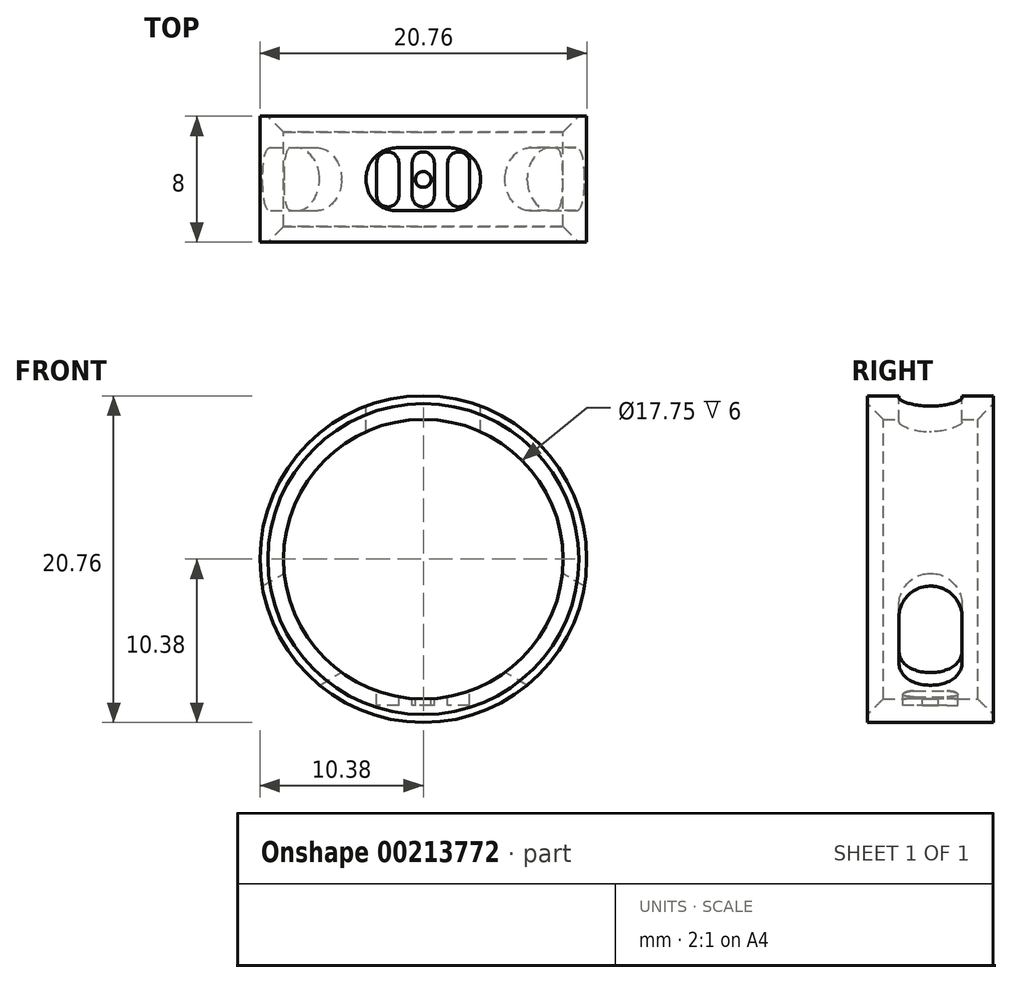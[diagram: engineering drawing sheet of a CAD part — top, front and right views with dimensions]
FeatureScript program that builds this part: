
annotation { "Feature Type Name" : "Feature", "Feature Type Description" : "" }
export const myFeature = defineFeature(function(context is Context, id is Id, definition is map)
    precondition{}
    {
        {
            var Q0;
            Q0=qCreatedBy(makeId("Front.planeOp"),FACE);
            var sketch = newSketch(context, id + "F0", { "sketchPlane" : qUnion([Q0])});
            skCircle(sketch, "E0", {"center": v(0, 0) * mm, "radius": 8.88 * mm});
            skCircle(sketch, "E1.0", {"center": v(0, 0) * mm, "radius": 10.38 * mm});
            skLineSegment(sketch, "E2.bottom", {"start": v(3.63, 9.72) * mm, "end": v(-3.63, 9.72) * mm, "construction": true});
            skLineSegment(sketch, "E2.top", {"start": v(3.63, 11.88) * mm, "end": v(-3.63, 11.88) * mm});
            skLineSegment(sketch, "E2.left", {"start": v(3.63, 9.72) * mm, "end": v(3.63, 11.88) * mm});
            skLineSegment(sketch, "E2.right", {"start": v(-3.63, 9.72) * mm, "end": v(-3.63, 11.88) * mm});
            skPoint(sketch, "E2.middle", {"position": v(0, 10.8) * mm});
            skLineSegment(sketch, "E3.1.0", {"start": v(-6.6, -8) * mm, "end": v(-8.47, -9.08) * mm});
            skLineSegment(sketch, "E3.1.1", {"start": v(-10.23, -1.71) * mm, "end": v(-12.1, -2.8) * mm});
            skLineSegment(sketch, "E3.1.2", {"start": v(-12.1, -2.8) * mm, "end": v(-8.47, -9.08) * mm});
            skLineSegment(sketch, "E3.1.3", {"start": v(-10.23, -1.71) * mm, "end": v(-6.6, -8) * mm, "construction": true});
            skLineSegment(sketch, "E3.2.0", {"start": v(10.23, -1.71) * mm, "end": v(12.1, -2.8) * mm});
            skLineSegment(sketch, "E3.2.1", {"start": v(6.6, -8) * mm, "end": v(8.47, -9.08) * mm});
            skLineSegment(sketch, "E3.2.2", {"start": v(8.47, -9.08) * mm, "end": v(12.1, -2.8) * mm});
            skLineSegment(sketch, "E3.2.3", {"start": v(6.6, -8) * mm, "end": v(10.23, -1.71) * mm, "construction": true});
            skLineSegment(sketch, "E4", {"start": v(0, 0) * mm, "end": v(7.34, 7.34) * mm, "construction": true});
            skLineSegment(sketch, "E5", {"start": v(0, 0) * mm, "end": v(-7.34, 7.34) * mm, "construction": true});
            skLineSegment(sketch, "E6.MirrorCS", {"start": v(0, 0) * mm, "end": v(7.34, -7.34) * mm, "construction": true});
            skLineSegment(sketch, "E7.MirrorCS", {"start": v(0, 0) * mm, "end": v(-7.34, -7.34) * mm, "construction": true});
            skLineSegment(sketch, "E8.0", {"start": v(-0.14, 0.14) * mm, "end": v(0, 0.28) * mm});
            skLineSegment(sketch, "E9.MirrorCS", {"start": v(0.14, -0.14) * mm, "end": v(0.28, 0) * mm});
            skLineSegment(sketch, "E10.MirrorCS", {"start": v(0.14, 0.14) * mm, "end": v(0, 0.28) * mm});
            skLineSegment(sketch, "E11.MirrorCS", {"start": v(-0.14, -0.14) * mm, "end": v(-0.28, 0) * mm});
            skLineSegment(sketch, "E12.MirrorCS", {"start": v(0.14, 0.14) * mm, "end": v(0.28, 0) * mm});
            skLineSegment(sketch, "E13.MirrorCS", {"start": v(-0.14, -0.14) * mm, "end": v(0, -0.28) * mm});
            skLineSegment(sketch, "E14.MirrorCS", {"start": v(0.14, -0.14) * mm, "end": v(0, -0.28) * mm});
            skLineSegment(sketch, "E15.MirrorCS", {"start": v(-0.14, 0.14) * mm, "end": v(-0.28, 0) * mm});
            skLineSegment(sketch, "E16.trimOffspring", {"start": v(-6.13, -6.42) * mm, "end": v(-7.2, -7.48) * mm, "construction": true});
            skLineSegment(sketch, "E17.trimOffspring", {"start": v(-6.42, -6.13) * mm, "end": v(-7.48, -7.2) * mm, "construction": true});
            skLineSegment(sketch, "E18.trimOffspring", {"start": v(-6.42, 6.13) * mm, "end": v(-7.48, 7.2) * mm, "construction": true});
            skLineSegment(sketch, "E19.trimOffspring", {"start": v(-6.13, 6.42) * mm, "end": v(-7.2, 7.48) * mm, "construction": true});
            skLineSegment(sketch, "E20.trimOffspring", {"start": v(6.13, 6.42) * mm, "end": v(7.2, 7.48) * mm, "construction": true});
            skLineSegment(sketch, "E21.trimOffspring", {"start": v(6.42, 6.13) * mm, "end": v(7.48, 7.2) * mm, "construction": true});
            skLineSegment(sketch, "E22.trimOffspring", {"start": v(6.13, -6.42) * mm, "end": v(7.2, -7.48) * mm, "construction": true});
            skLineSegment(sketch, "E23.trimOffspring", {"start": v(6.42, -6.13) * mm, "end": v(7.48, -7.2) * mm, "construction": true});
            skLineSegment(sketch, "E24", {"start": v(-3.63, 9.72) * mm, "end": v(-3.63, 6.6) * mm});
            skLineSegment(sketch, "E25", {"start": v(-3.63, 6.6) * mm, "end": v(3.63, 6.6) * mm});
            skLineSegment(sketch, "E26", {"start": v(3.63, 6.6) * mm, "end": v(3.63, 9.72) * mm});
            skLineSegment(sketch, "E27", {"start": v(10.23, -1.71) * mm, "end": v(7.27, 0) * mm});
            skLineSegment(sketch, "E28", {"start": v(6.6, -8) * mm, "end": v(3.35, -6.13) * mm});
            skLineSegment(sketch, "E29", {"start": v(3.35, -6.13) * mm, "end": v(7.27, 0) * mm});
            skLineSegment(sketch, "E30", {"start": v(-6.6, -8) * mm, "end": v(-3.28, -6.1) * mm});
            skLineSegment(sketch, "E31", {"start": v(-10.23, -1.71) * mm, "end": v(-6.86, 0.24) * mm});
            skLineSegment(sketch, "E32", {"start": v(-6.86, 0.24) * mm, "end": v(-3.28, -6.1) * mm});
            skSolve(sketch);
        }
        {
            var Q0;
            Q0=makeQuery(id+"F0.imprint","IMPRINT",FACE,{"disambiguationData":[TD([[makeQuery(id+"F0.imprint","IMPRINT",EDGE,{"derivedFrom":sQuery(id+"F0.wireOp",EDGE,"E0")}),-1.0]])]});
            var Q1;
            {var subQ2=sQuery(id+"F0.wireOp",EDGE,"E16.trimOffspring");var subQ7=sQuery(id+"F0.wireOp",EDGE,"E0");var subQ9=makeQuery(id+"F0.imprint","INTERSECT",VERTEX,{"derivedFrom":[subQ7,subQ2]});Q1=makeQuery(id+"F0.imprint","IMPRINT",FACE,{"disambiguationData":[TD([[makeQuery(id+"F0.imprint","IMPRINT",EDGE,{"disambiguationData":[TD([[subQ9,-1.0]])],"derivedFrom":subQ7}),-1.0]])]});}
            var Q2;
            {var subQ5=sQuery(id+"F0.wireOp",EDGE,"E21.trimOffspring");var subQ7=sQuery(id+"F0.wireOp",EDGE,"E0");var subQ8=makeQuery(id+"F0.imprint","INTERSECT",VERTEX,{"derivedFrom":[subQ7,subQ5]});Q2=makeQuery(id+"F0.imprint","IMPRINT",FACE,{"disambiguationData":[TD([[makeQuery(id+"F0.imprint","IMPRINT",EDGE,{"disambiguationData":[TD([[subQ8,1.0]])],"derivedFrom":subQ7}),-1.0]])]});}
            var Q3;
            {var subQ2=sQuery(id+"F0.wireOp",EDGE,"E19.trimOffspring");var subQ7=sQuery(id+"F0.wireOp",EDGE,"E0");var subQ8=makeQuery(id+"F0.imprint","INTERSECT",VERTEX,{"derivedFrom":[subQ7,subQ2]});Q3=makeQuery(id+"F0.imprint","IMPRINT",FACE,{"disambiguationData":[TD([[makeQuery(id+"F0.imprint","IMPRINT",EDGE,{"disambiguationData":[TD([[subQ8,1.0]])],"derivedFrom":subQ7}),-1.0]])]});}
            var Q4;
            {var subQ5=sQuery(id+"F0.wireOp",EDGE,"E17.trimOffspring");var subQ6=sQuery(id+"F0.wireOp",EDGE,"E0");var subQ7=makeQuery(id+"F0.imprint","INTERSECT",VERTEX,{"derivedFrom":[subQ6,subQ5]});Q4=makeQuery(id+"F0.imprint","IMPRINT",FACE,{"disambiguationData":[TD([[makeQuery(id+"F0.imprint","IMPRINT",EDGE,{"disambiguationData":[TD([[subQ7,1.0]])],"derivedFrom":subQ6}),-1.0]])]});}
            extrude(context, id + "F1", {"entities" : qUnion([Q0, Q1, Q2, Q3, Q4]), "depth" : 4 * mm, "hasSecondDirection" : true, "secondDirectionOppositeDirection" : true, "secondDirectionDepth" : 4 * mm});
        }
        {
            var Q0;
            Q0=makeQuery(id+"F1.opExtrude","CAP_EDGE",EDGE,{"disambiguationData":[OSD([sQuery(id+"F0.wireOp",EDGE,"E0")])],"isStart":false});
            var Q1;
            Q1=makeQuery(id+"F1.opExtrude","CAP_EDGE",EDGE,{"disambiguationData":[OSD([sQuery(id+"F0.wireOp",EDGE,"E0")])],"isStart":true});
            chamfer(context, id + "F2", {"entities" : qUnion([Q0, Q1]), "width" : 1 * mm, "tangentPropagation" : true});
        }
        {
            var Q0;
            Q0=qCreatedBy(makeId("Top.planeOp"),FACE);
            var sketch = newSketch(context, id + "F3", { "sketchPlane" : qUnion([Q0])});
            skCircle(sketch, "E33", {"center": v(0, 0) * mm, "radius": 0.15 * mm});
            skCircle(sketch, "E34.1.0.0", {"center": v(0, -0.6) * mm, "radius": 0.15 * mm});
            skCircle(sketch, "E34.2.0.0", {"center": v(0, -1.2) * mm, "radius": 0.15 * mm});
            skCircle(sketch, "E34.3.0.0", {"center": v(0, -1.8) * mm, "radius": 0.15 * mm});
            skCircle(sketch, "E34.4.0.0", {"center": v(0, -2.4) * mm, "radius": 0.15 * mm});
            skCircle(sketch, "E34.5.0.0", {"center": v(0, -3) * mm, "radius": 0.15 * mm});
            skCircle(sketch, "E34.6.0.0", {"center": v(0, -3.6) * mm, "radius": 0.15 * mm});
            skLineSegment(sketch, "E34.direction1", {"start": v(0, 0) * mm, "end": v(0, -0.6) * mm, "construction": true});
            skCircle(sketch, "E35.MirrorC", {"center": v(0, 0.6) * mm, "radius": 0.15 * mm});
            skCircle(sketch, "E36.MirrorC", {"center": v(0, 1.2) * mm, "radius": 0.15 * mm});
            skCircle(sketch, "E37.MirrorC", {"center": v(0, 1.8) * mm, "radius": 0.15 * mm});
            skCircle(sketch, "E38.MirrorC", {"center": v(0, 2.4) * mm, "radius": 0.15 * mm});
            skCircle(sketch, "E39.MirrorC", {"center": v(0, 3) * mm, "radius": 0.15 * mm});
            skCircle(sketch, "E40.MirrorC", {"center": v(0, 3.6) * mm, "radius": 0.15 * mm});
            skSolve(sketch);
        }
        {
            var Q0;
            Q0=makeQuery(id+"F0.imprint","IMPRINT",FACE,{"disambiguationData":[TD([[makeQuery(id+"F0.imprint","IMPRINT",EDGE,{"derivedFrom":sQuery(id+"F0.wireOp",EDGE,"E2.top")}),1.0]])]});
            var Q1;
            {var subQ0=sQuery(id+"F0.wireOp",EDGE,"E24");var subQ1=sQuery(id+"F0.wireOp",EDGE,"E0");var subQ2=makeQuery(id+"F0.imprint","INTERSECT",VERTEX,{"derivedFrom":[subQ1,subQ0]});Q1=makeQuery(id+"F0.imprint","IMPRINT",FACE,{"disambiguationData":[TD([[makeQuery(id+"F0.imprint","IMPRINT",EDGE,{"disambiguationData":[TD([[subQ2,1.0]])],"derivedFrom":subQ1}),-1.0]])]});}
            var Q2;
            {var subQ5=sQuery(id+"F0.wireOp",EDGE,"E25");Q2=makeQuery(id+"F0.imprint","IMPRINT",FACE,{"disambiguationData":[TD([[makeQuery(id+"F0.imprint","IMPRINT",EDGE,{"derivedFrom":subQ5}),1.0]])]});}
            var Q3;
            {var subQ5=sQuery(id+"F0.wireOp",EDGE,"E29");Q3=makeQuery(id+"F0.imprint","IMPRINT",FACE,{"disambiguationData":[TD([[makeQuery(id+"F0.imprint","IMPRINT",EDGE,{"derivedFrom":subQ5}),-1.0]])]});}
            var Q4;
            {var subQ0=sQuery(id+"F0.wireOp",EDGE,"E28");var subQ1=sQuery(id+"F0.wireOp",EDGE,"E0");var subQ2=makeQuery(id+"F0.imprint","INTERSECT",VERTEX,{"derivedFrom":[subQ1,subQ0]});Q4=makeQuery(id+"F0.imprint","IMPRINT",FACE,{"disambiguationData":[TD([[makeQuery(id+"F0.imprint","IMPRINT",EDGE,{"disambiguationData":[TD([[subQ2,-1.0]])],"derivedFrom":subQ1}),-1.0]])]});}
            var Q5;
            {var subQ0=sQuery(id+"F0.wireOp",EDGE,"E3.2.0");Q5=makeQuery(id+"F0.imprint","IMPRINT",FACE,{"disambiguationData":[TD([[makeQuery(id+"F0.imprint","IMPRINT",EDGE,{"derivedFrom":subQ0}),-1.0]])]});}
            var Q6;
            {var subQ5=sQuery(id+"F0.wireOp",EDGE,"E32");Q6=makeQuery(id+"F0.imprint","IMPRINT",FACE,{"disambiguationData":[TD([[makeQuery(id+"F0.imprint","IMPRINT",EDGE,{"derivedFrom":subQ5}),-1.0]])]});}
            var Q7;
            {var subQ0=sQuery(id+"F0.wireOp",EDGE,"E3.1.0");Q7=makeQuery(id+"F0.imprint","IMPRINT",FACE,{"disambiguationData":[TD([[makeQuery(id+"F0.imprint","IMPRINT",EDGE,{"derivedFrom":subQ0}),-1.0]])]});}
            var Q8;
            {var subQ0=sQuery(id+"F0.wireOp",EDGE,"E31");var subQ1=sQuery(id+"F0.wireOp",EDGE,"E0");var subQ2=makeQuery(id+"F0.imprint","INTERSECT",VERTEX,{"derivedFrom":[subQ1,subQ0]});Q8=makeQuery(id+"F0.imprint","IMPRINT",FACE,{"disambiguationData":[TD([[makeQuery(id+"F0.imprint","IMPRINT",EDGE,{"disambiguationData":[TD([[subQ2,-1.0]])],"derivedFrom":subQ1}),-1.0]])]});}
            extrude(context, id + "F4", {"entities" : qUnion([Q0, Q1, Q2, Q3, Q4, Q5, Q6, Q7, Q8]), "operationType" : NewBodyOperationType.REMOVE, "oppositeDirection" : true, "depth" : 2 * mm, "hasSecondDirection" : true, "secondDirectionOppositeDirection" : false, "secondDirectionDepth" : 2 * mm});
        }
        {
            var Q0;
            Q0=makeQuery(id+"F4.boolean.opBoolean","COPY",EDGE,{"derivedFrom":makeQuery(id+"F4.opExtrude","CAP_EDGE",EDGE,{"disambiguationData":[OSD([sQuery(id+"F0.wireOp",EDGE,"E3.2.1"),sQuery(id+"F0.wireOp",EDGE,"E28")])],"isStart":false})});
            var Q1;
            Q1=makeQuery(id+"F4.boolean.opBoolean","COPY",EDGE,{"derivedFrom":makeQuery(id+"F4.opExtrude","CAP_EDGE",EDGE,{"disambiguationData":[OSD([sQuery(id+"F0.wireOp",EDGE,"E3.2.0"),sQuery(id+"F0.wireOp",EDGE,"E27")])],"isStart":false})});
            var Q2;
            Q2=makeQuery(id+"F4.boolean.opBoolean","COPY",EDGE,{"derivedFrom":makeQuery(id+"F4.opExtrude","CAP_EDGE",EDGE,{"disambiguationData":[OSD([sQuery(id+"F0.wireOp",EDGE,"E3.2.0"),sQuery(id+"F0.wireOp",EDGE,"E27")])],"isStart":true})});
            var Q3;
            Q3=makeQuery(id+"F4.boolean.opBoolean","COPY",EDGE,{"derivedFrom":makeQuery(id+"F4.opExtrude","CAP_EDGE",EDGE,{"disambiguationData":[OSD([sQuery(id+"F0.wireOp",EDGE,"E3.2.1"),sQuery(id+"F0.wireOp",EDGE,"E28")])],"isStart":true})});
            var Q4;
            Q4=makeQuery(id+"F4.boolean.opBoolean","COPY",EDGE,{"derivedFrom":makeQuery(id+"F4.opExtrude","CAP_EDGE",EDGE,{"disambiguationData":[OSD([sQuery(id+"F0.wireOp",EDGE,"E3.1.0"),sQuery(id+"F0.wireOp",EDGE,"E30")])],"isStart":false})});
            var Q5;
            Q5=makeQuery(id+"F4.boolean.opBoolean","COPY",EDGE,{"derivedFrom":makeQuery(id+"F4.opExtrude","CAP_EDGE",EDGE,{"disambiguationData":[OSD([sQuery(id+"F0.wireOp",EDGE,"E3.1.1"),sQuery(id+"F0.wireOp",EDGE,"E31")])],"isStart":false})});
            var Q6;
            Q6=makeQuery(id+"F4.boolean.opBoolean","COPY",EDGE,{"derivedFrom":makeQuery(id+"F4.opExtrude","CAP_EDGE",EDGE,{"disambiguationData":[OSD([sQuery(id+"F0.wireOp",EDGE,"E3.1.1"),sQuery(id+"F0.wireOp",EDGE,"E31")])],"isStart":true})});
            var Q7;
            Q7=makeQuery(id+"F4.boolean.opBoolean","COPY",EDGE,{"derivedFrom":makeQuery(id+"F4.opExtrude","CAP_EDGE",EDGE,{"disambiguationData":[OSD([sQuery(id+"F0.wireOp",EDGE,"E3.1.0"),sQuery(id+"F0.wireOp",EDGE,"E30")])],"isStart":true})});
            var Q8;
            Q8=makeQuery(id+"F4.boolean.opBoolean","COPY",EDGE,{"derivedFrom":makeQuery(id+"F4.opExtrude","CAP_EDGE",EDGE,{"disambiguationData":[OSD([sQuery(id+"F0.wireOp",EDGE,"E2.right"),sQuery(id+"F0.wireOp",EDGE,"E24")])],"isStart":false})});
            var Q9;
            Q9=makeQuery(id+"F4.boolean.opBoolean","COPY",EDGE,{"derivedFrom":makeQuery(id+"F4.opExtrude","CAP_EDGE",EDGE,{"disambiguationData":[OSD([sQuery(id+"F0.wireOp",EDGE,"E2.left"),sQuery(id+"F0.wireOp",EDGE,"E26")])],"isStart":false})});
            var Q10;
            Q10=makeQuery(id+"F4.boolean.opBoolean","COPY",EDGE,{"derivedFrom":makeQuery(id+"F4.opExtrude","CAP_EDGE",EDGE,{"disambiguationData":[OSD([sQuery(id+"F0.wireOp",EDGE,"E2.right"),sQuery(id+"F0.wireOp",EDGE,"E24")])],"isStart":true})});
            var Q11;
            Q11=makeQuery(id+"F4.boolean.opBoolean","COPY",EDGE,{"derivedFrom":makeQuery(id+"F4.opExtrude","CAP_EDGE",EDGE,{"disambiguationData":[OSD([sQuery(id+"F0.wireOp",EDGE,"E2.left"),sQuery(id+"F0.wireOp",EDGE,"E26")])],"isStart":true})});
            fillet(context, id + "F5", {"entities" : qUnion([Q0, Q1, Q2, Q3, Q4, Q5, Q6, Q7, Q8, Q9, Q10, Q11]), "radius" : 1.94 * mm, "tangentPropagation" : true, "allowEdgeOverflow" : false});
        }
        {
            var Q0;
            Q0=qCreatedBy(makeId("Top.planeOp"),FACE);
            var sketch = newSketch(context, id + "F6", { "sketchPlane" : qUnion([Q0])});
            skLineSegment(sketch, "E41.bottom", {"start": v(-0.7, 1.04) * mm, "end": v(-0.7, -1.05) * mm});
            skArc(sketch, "E42.filletArc", {"start": v(0.7, 1.04) * mm, "mid": v(0.49, 1.54) * mm, "end": v(0, 1.74) * mm});
            skArc(sketch, "E43.filletArc", {"start": v(0, 1.74) * mm, "mid": v(-0.5, 1.54) * mm, "end": v(-0.7, 1.04) * mm});
            skArc(sketch, "E44.filletArc", {"start": v(0, -1.75) * mm, "mid": v(0.49, -1.54) * mm, "end": v(0.7, -1.05) * mm});
            skArc(sketch, "E45.filletArc", {"start": v(-0.7, -1.05) * mm, "mid": v(-0.5, -1.54) * mm, "end": v(0, -1.75) * mm});
            skLineSegment(sketch, "E46.bottom", {"start": v(-2.96, 1.04) * mm, "end": v(-2.96, -1.05) * mm});
            skLineSegment(sketch, "E46.top", {"start": v(-1.56, 1.04) * mm, "end": v(-1.56, -1.05) * mm});
            skArc(sketch, "E47.filletArc", {"start": v(-1.56, 1.04) * mm, "mid": v(-1.76, 1.54) * mm, "end": v(-2.26, 1.74) * mm});
            skArc(sketch, "E48.filletArc", {"start": v(-2.26, 1.74) * mm, "mid": v(-2.75, 1.54) * mm, "end": v(-2.96, 1.04) * mm});
            skArc(sketch, "E49.filletArc", {"start": v(-2.26, -1.75) * mm, "mid": v(-1.76, -1.54) * mm, "end": v(-1.56, -1.05) * mm});
            skArc(sketch, "E50.filletArc", {"start": v(-2.96, -1.05) * mm, "mid": v(-2.75, -1.54) * mm, "end": v(-2.26, -1.75) * mm});
            skLineSegment(sketch, "E51", {"start": v(0.7, 1.04) * mm, "end": v(0.7, -1.05) * mm});
            skCircle(sketch, "E52", {"center": v(0, 0) * mm, "radius": 0.5 * mm});
            skLineSegment(sketch, "E53.bottom", {"start": v(1.55, 1.04) * mm, "end": v(1.55, -1.05) * mm});
            skLineSegment(sketch, "E53.top", {"start": v(2.95, 1.04) * mm, "end": v(2.95, -1.05) * mm});
            skArc(sketch, "E54.filletArc", {"start": v(2.95, 1.04) * mm, "mid": v(2.74, 1.54) * mm, "end": v(2.25, 1.74) * mm});
            skArc(sketch, "E55.filletArc", {"start": v(2.25, 1.74) * mm, "mid": v(1.75, 1.54) * mm, "end": v(1.55, 1.04) * mm});
            skArc(sketch, "E56.filletArc", {"start": v(2.25, -1.75) * mm, "mid": v(2.74, -1.54) * mm, "end": v(2.95, -1.05) * mm});
            skArc(sketch, "E57.filletArc", {"start": v(1.55, -1.05) * mm, "mid": v(1.75, -1.54) * mm, "end": v(2.25, -1.75) * mm});
            skSolve(sketch);
        }
        {
            var Q0;
            Q0=makeQuery(id+"F6.imprint","IMPRINT",FACE,{"disambiguationData":[TD([[makeQuery(id+"F6.imprint","IMPRINT",EDGE,{"derivedFrom":sQuery(id+"F6.wireOp",EDGE,"E53.bottom")}),1.0]])]});
            var Q1;
            Q1=makeQuery(id+"F6.imprint","IMPRINT",FACE,{"disambiguationData":[TD([[makeQuery(id+"F6.imprint","IMPRINT",EDGE,{"derivedFrom":sQuery(id+"F6.wireOp",EDGE,"E41.bottom")}),1.0]])]});
            var Q2;
            Q2=makeQuery(id+"F6.imprint","IMPRINT",FACE,{"disambiguationData":[TD([[makeQuery(id+"F6.imprint","IMPRINT",EDGE,{"derivedFrom":sQuery(id+"F6.wireOp",EDGE,"E46.bottom")}),1.0]])]});
            extrude(context, id + "F7", {"entities" : qUnion([Q0, Q1, Q2]), "operationType" : NewBodyOperationType.REMOVE, "oppositeDirection" : true, "depth" : 9.3 * mm, "offsetDistance" : 25 * mm});
        }
    });
